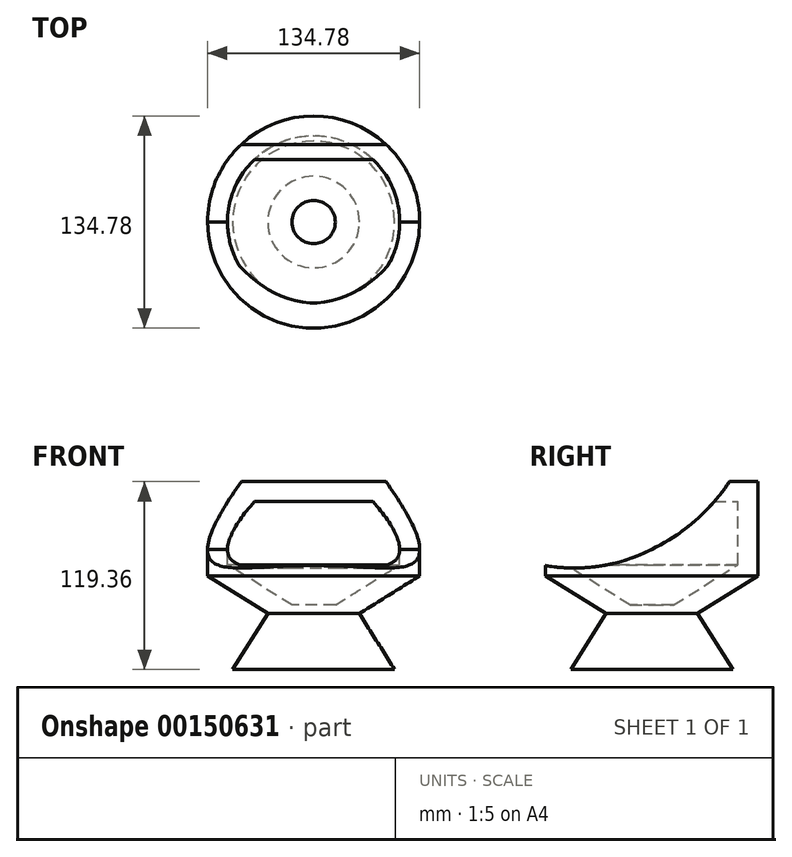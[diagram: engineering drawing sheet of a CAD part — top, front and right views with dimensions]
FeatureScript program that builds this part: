
annotation { "Feature Type Name" : "Feature", "Feature Type Description" : "" }
export const myFeature = defineFeature(function(context is Context, id is Id, definition is map)
    precondition{}
    {
        {
            var Q0;
            Q0=qCreatedBy(makeId("Front.planeOp"),FACE);
            var sketch = newSketch(context, id + "F0", { "sketchPlane" : qUnion([Q0])});
            skLineSegment(sketch, "E0", {"start": v(0, -35.54) * mm, "end": v(-51.41, -35.54) * mm});
            skLineSegment(sketch, "E1", {"start": v(-51.41, -35.54) * mm, "end": v(-29.1, 0) * mm});
            skLineSegment(sketch, "E2", {"start": v(-29.1, 0) * mm, "end": v(-67.39, 24.04) * mm});
            skLineSegment(sketch, "E3", {"start": v(-67.39, 24.04) * mm, "end": v(-67.39, 44.4) * mm});
            skLineSegment(sketch, "E4", {"start": v(-67.39, 44.4) * mm, "end": v(0, 44.4) * mm});
            skLineSegment(sketch, "E5", {"start": v(0, 44.4) * mm, "end": v(0, -35.54) * mm});
            skSolve(sketch);
        }
        {
            var Q0;
            Q0 = qSketchRegion(id + "F0", true);
            var Q1;
            Q1=sQuery(id+"F0.wireOp",EDGE,"E5");
            revolve(context, id + "F1", {"entities" : qUnion([Q0]), "axis" : qUnion([Q1]), "revolveType" : RevolveType.FULL});
        }
        {
            var Q0;
            Q0=makeQuery(id+"F1.opRevolve","SWEPT_FACE",FACE,{"disambiguationData":[OSD([sQuery(id+"F0.wireOp",EDGE,"E4")])]});
            extrude(context, id + "F2", {"entities" : qUnion([Q0]), "operationType" : NewBodyOperationType.ADD, "depth" : 39.4 * mm});
        }
        {
            var Q0;
            Q0=qCreatedBy(makeId("Right.planeOp"),FACE);
            var sketch = newSketch(context, id + "F3", { "sketchPlane" : qUnion([Q0])});
            skArc(sketch, "E6", {"start": v(-68.45, 30.63) * mm, "mid": v(-33.4, 30.13) * mm, "end": v(0, 40.8) * mm});
            skArc(sketch, "E7", {"start": v(0, 40.8) * mm, "mid": v(28.7, 59.99) * mm, "end": v(50.98, 86.34) * mm});
            skLineSegment(sketch, "E8", {"start": v(50.98, 86.34) * mm, "end": v(-68.07, 86.34) * mm});
            skLineSegment(sketch, "E9", {"start": v(-68.07, 86.34) * mm, "end": v(-68.45, 30.63) * mm});
            skSolve(sketch);
        }
        {
            var Q0;
            Q0 = qSketchRegion(id + "F3", true);
            extrude(context, id + "F4", {"entities" : qUnion([Q0]), "operationType" : NewBodyOperationType.REMOVE, "endBound" : BoundingType.SYMMETRIC, "oppositeDirection" : true, "depth" : 156.45 * mm});
        }
        {
            var Q0;
            Q0=makeQuery(id+"F4.boolean.opBoolean","COPY",FACE,{"derivedFrom":makeQuery(id+"F4.opExtrude","SWEPT_FACE",FACE,{"disambiguationData":[OSD([sQuery(id+"F3.wireOp",EDGE,"E6")])]})});
            var Q1;
            Q1=makeQuery(id+"F4.boolean.opBoolean","COPY",FACE,{"derivedFrom":makeQuery(id+"F4.opExtrude","SWEPT_FACE",FACE,{"disambiguationData":[OSD([sQuery(id+"F3.wireOp",EDGE,"E7")])]})});
            shell(context, id + "F5", {"entities" : qUnion([Q0, Q1]), "thickness" : 12.7 * mm});
        }
        {
            var Q0;
            Q0=makeQuery(id+"F5.opShell","OFFSET_FACE",FACE,{"disambiguationData":[OSD([sQuery(id+"F0.wireOp",EDGE,"E0")])]});
            extrude(context, id + "F6", {"entities" : qUnion([Q0]), "operationType" : NewBodyOperationType.ADD, "depth" : 28.2 * mm});
        }
    });
